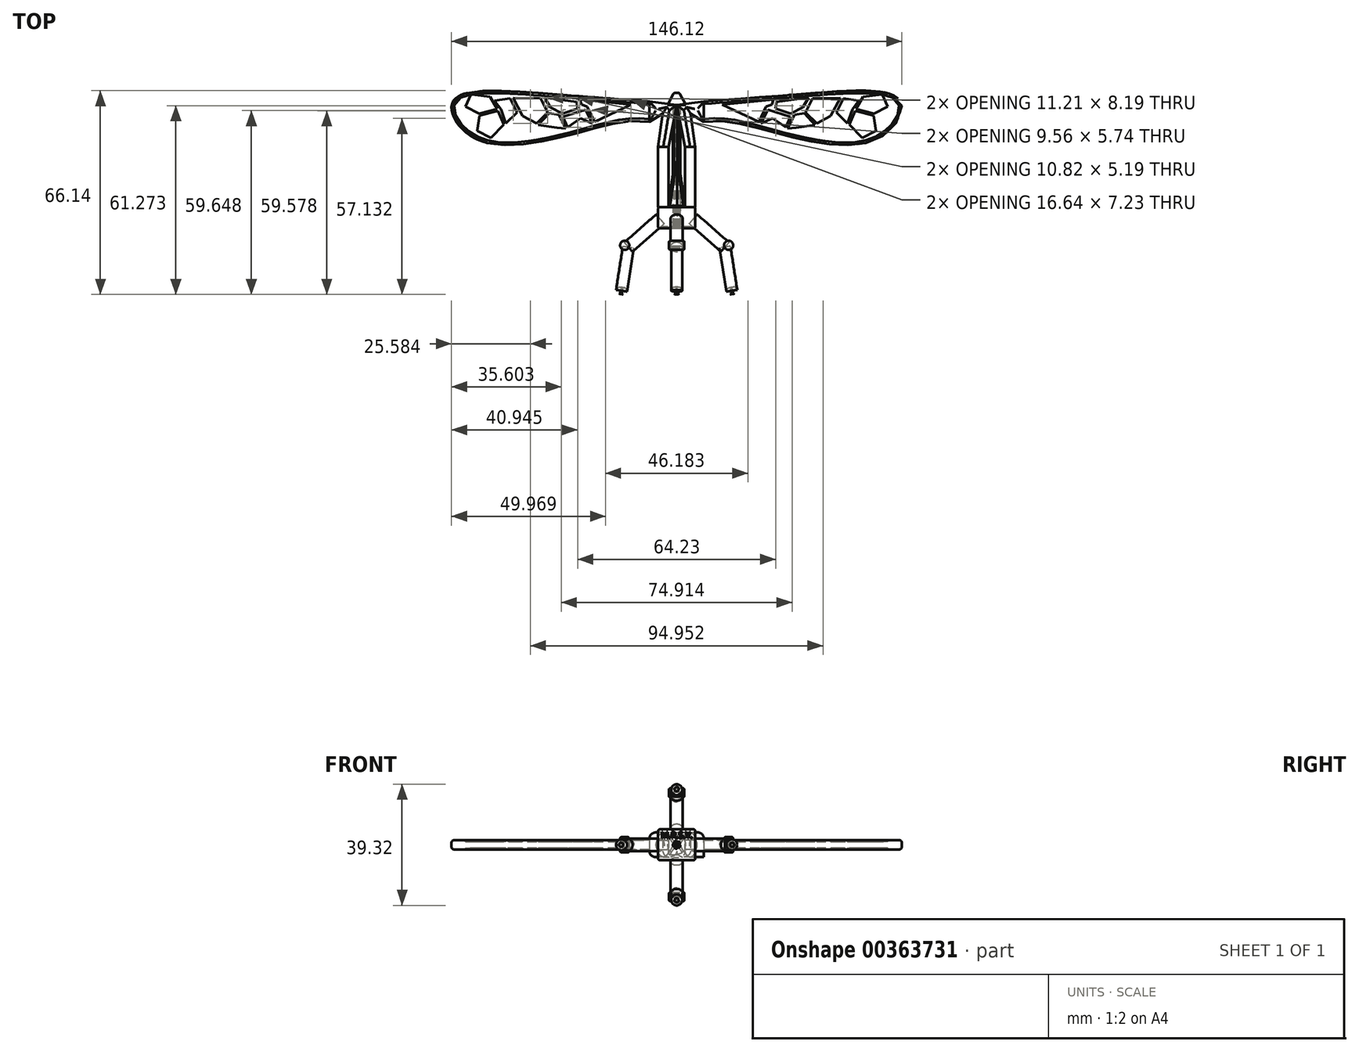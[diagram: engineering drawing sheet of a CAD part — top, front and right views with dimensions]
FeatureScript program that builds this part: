
annotation { "Feature Type Name" : "Feature", "Feature Type Description" : "" }
export const myFeature = defineFeature(function(context is Context, id is Id, definition is map)
    precondition{}
    {
        {
            var Q0;
            Q0=qCreatedBy(makeId("Top.planeOp"),FACE);
            var sketch = newSketch(context, id + "F0", { "sketchPlane" : qUnion([Q0])});
            skLineSegment(sketch, "E0.bottom", {"start": v(-6, 3.87) * mm, "end": v(0, 3.87) * mm});
            skLineSegment(sketch, "E0.top", {"start": v(-6, -3.02) * mm, "end": v(0, -3.02) * mm});
            skLineSegment(sketch, "E0.left", {"start": v(-6, 3.87) * mm, "end": v(-6, -3.02) * mm});
            skLineSegment(sketch, "E0.right", {"start": v(0, 3.87) * mm, "end": v(0, -3.02) * mm});
            skLineSegment(sketch, "E1", {"start": v(-6, 3.87) * mm, "end": v(-6, 23.41) * mm});
            skLineSegment(sketch, "E2", {"start": v(-6, 23.41) * mm, "end": v(-2.68, 23.41) * mm});
            skLineSegment(sketch, "E3", {"start": v(-2.68, 23.41) * mm, "end": v(-2.68, 3.87) * mm});
            skLineSegment(sketch, "E4", {"start": v(-6, 23.41) * mm, "end": v(-4.5, 34.28) * mm});
            skLineSegment(sketch, "E5", {"start": v(-4.5, 34.28) * mm, "end": v(-8.84, 31.63) * mm});
            skLineSegment(sketch, "E6", {"start": v(-8.84, 31.63) * mm, "end": v(-8.84, 38.19) * mm});
            skLineSegment(sketch, "E7", {"start": v(-8.84, 38.19) * mm, "end": v(0, 36.98) * mm});
            skLineSegment(sketch, "E8", {"start": v(-2.68, 23.41) * mm, "end": v(0, 36.98) * mm});
            skLineSegment(sketch, "E9.MirrorCS", {"start": v(6, 3.87) * mm, "end": v(0, 3.87) * mm});
            skLineSegment(sketch, "E10.MirrorCS", {"start": v(2.68, 23.41) * mm, "end": v(0, 36.98) * mm});
            skLineSegment(sketch, "E11.MirrorCS", {"start": v(6, -3.02) * mm, "end": v(0, -3.02) * mm});
            skLineSegment(sketch, "E12.MirrorCS", {"start": v(8.84, 38.19) * mm, "end": v(0, 36.98) * mm});
            skLineSegment(sketch, "E13.MirrorCS", {"start": v(6, 3.87) * mm, "end": v(6, -3.02) * mm});
            skLineSegment(sketch, "E14.MirrorCS", {"start": v(4.5, 34.28) * mm, "end": v(8.84, 31.63) * mm});
            skLineSegment(sketch, "E15.MirrorCS", {"start": v(8.84, 31.63) * mm, "end": v(8.84, 38.19) * mm});
            skLineSegment(sketch, "E16.MirrorCS", {"start": v(6, 23.41) * mm, "end": v(4.5, 34.28) * mm});
            skLineSegment(sketch, "E17.MirrorCS", {"start": v(6, 3.87) * mm, "end": v(6, 23.41) * mm});
            skLineSegment(sketch, "E18.MirrorCS", {"start": v(6, 23.41) * mm, "end": v(2.68, 23.41) * mm});
            skLineSegment(sketch, "E19.MirrorCS", {"start": v(2.68, 23.41) * mm, "end": v(2.68, 3.87) * mm});
            skFitSpline(sketch, "E20", {"points": [v(-8.84, 38.19) * mm, v(-45.9, 40.99) * mm, v(-72.58, 38.19) * mm, v(-63.04, 25.19) * mm, v(-19.97, 31.15) * mm, v(-8.84, 31.63) * mm], "startDerivative": vector(-146.25, 11.04) * mm, "endDerivative": vector(65.13, -7.24) * mm});
            skFitSpline(sketch, "E21.MirrorCS", {"points": [v(8.84, 38.19) * mm, v(45.9, 40.99) * mm, v(72.58, 38.19) * mm, v(63.04, 25.19) * mm, v(19.97, 31.15) * mm, v(8.84, 31.63) * mm], "startDerivative": vector(146.25, 11.04) * mm, "endDerivative": vector(-65.13, -7.24) * mm});
            skLineSegment(sketch, "E22", {"start": v(0, 3.87) * mm, "end": v(0, 18.7) * mm});
            skLineSegment(sketch, "E23", {"start": v(0, 18.7) * mm, "end": v(-0.65, 18.7) * mm});
            skLineSegment(sketch, "E24", {"start": v(0, 18.7) * mm, "end": v(0.65, 18.7) * mm});
            skLineSegment(sketch, "E25", {"start": v(-2.68, 3.87) * mm, "end": v(-0.65, 18.7) * mm});
            skLineSegment(sketch, "E26", {"start": v(2.68, 3.87) * mm, "end": v(0.65, 18.7) * mm});
            skSolve(sketch);
        }
        {
            var Q0;
            Q0=makeQuery(id+"F0.imprint","IMPRINT",FACE,{"disambiguationData":[TD([[makeQuery(id+"F0.imprint","IMPRINT",EDGE,{"derivedFrom":sQuery(id+"F0.wireOp",EDGE,"E2")}),1.0]])]});
            var Q1;
            Q1=makeQuery(id+"F0.imprint","IMPRINT",FACE,{"disambiguationData":[TD([[makeQuery(id+"F0.imprint","IMPRINT",EDGE,{"derivedFrom":sQuery(id+"F0.wireOp",EDGE,"E10.MirrorCS")}),-1.0]])]});
            extrude(context, id + "F1", {"entities" : qUnion([Q0, Q1]), "endBound" : BoundingType.SYMMETRIC, "depth" : 8 * mm});
        }
        {
            var Q0;
            {var subQ3=sQuery(id+"F0.wireOp",EDGE,"2m0UVoe8-9YMW-rYIg-5lbe-QnaoNtSdkHYh");Q0=makeQuery(id+"F0.imprint","IMPRINT",FACE,{"disambiguationData":[TD([[makeQuery(id+"F0.imprint","IMPRINT",EDGE,{"derivedFrom":subQ3}),-1.0]])]});}
            var Q1;
            {var subQ0=sQuery(id+"F0.wireOp",EDGE,"E1");Q1=makeQuery(id+"F0.imprint","IMPRINT",FACE,{"disambiguationData":[TD([[makeQuery(id+"F0.imprint","IMPRINT",EDGE,{"derivedFrom":subQ0}),-1.0]])]});}
            var Q2;
            {var subQ0=sQuery(id+"F0.wireOp",EDGE,"E17.MirrorCS");Q2=makeQuery(id+"F0.imprint","IMPRINT",FACE,{"disambiguationData":[TD([[makeQuery(id+"F0.imprint","IMPRINT",EDGE,{"derivedFrom":subQ0}),1.0]])]});}
            extrude(context, id + "F2", {"entities" : qUnion([Q0, Q1, Q2]), "endBound" : BoundingType.SYMMETRIC, "depth" : 3 * mm});
        }
        {
            var Q0;
            Q0=makeQuery(id+"F0.imprint","IMPRINT",FACE,{"disambiguationData":[TD([[makeQuery(id+"F0.imprint","IMPRINT",EDGE,{"derivedFrom":sQuery(id+"F0.wireOp",EDGE,"E0.top")}),1.0]])]});
            var Q1;
            Q1=makeQuery(id+"F0.imprint","IMPRINT",FACE,{"disambiguationData":[TD([[makeQuery(id+"F0.imprint","IMPRINT",EDGE,{"derivedFrom":sQuery(id+"F0.wireOp",EDGE,"E11.MirrorCS")}),-1.0]])]});
            extrude(context, id + "F3", {"entities" : qUnion([Q0, Q1]), "endBound" : BoundingType.SYMMETRIC, "depth" : 10 * mm});
        }
        {
            var Q0;
            {var subQ0=sQuery(id+"F0.wireOp",EDGE,"E22");Q0=makeQuery(id+"F0.imprint","IMPRINT",FACE,{"disambiguationData":[TD([[makeQuery(id+"F0.imprint","IMPRINT",EDGE,{"derivedFrom":subQ0}),1.0]])]});}
            var Q1;
            {var subQ0=sQuery(id+"F0.wireOp",EDGE,"E22");Q1=makeQuery(id+"F0.imprint","IMPRINT",FACE,{"disambiguationData":[TD([[makeQuery(id+"F0.imprint","IMPRINT",EDGE,{"derivedFrom":subQ0}),-1.0]])]});}
            var Q2;
            Q2=sQuery(id+"F0.wireOp",EDGE,"E24");
            revolve(context, id + "F4", {"entities" : qUnion([Q0, Q1]), "axis" : qUnion([Q2]), "revolveType" : RevolveType.SYMMETRIC, "angle" : 25 * degree});
        }
        {
            var Q0;
            Q0=makeQuery(id+"F3.opExtrude","SWEPT_FACE",FACE,{"disambiguationData":[OSD([sQuery(id+"F0.wireOp",EDGE,"E0.top"),sQuery(id+"F0.wireOp",EDGE,"E11.MirrorCS")])]});
            var sketch = newSketch(context, id + "F5", { "sketchPlane" : qUnion([Q0])});
            skCircle(sketch, "E27.cCircle", {"center": v(0, 0) * mm, "radius": 0.63 * mm, "construction": true});
            skLineSegment(sketch, "E27.0", {"start": v(-0.32, 0.7) * mm, "end": v(0.58, 0.52) * mm});
            skLineSegment(sketch, "E27.1", {"start": v(0.58, 0.52) * mm, "end": v(0.68, -0.39) * mm});
            skLineSegment(sketch, "E27.2", {"start": v(0.68, -0.39) * mm, "end": v(-0.16, -0.76) * mm});
            skLineSegment(sketch, "E27.3", {"start": v(-0.16, -0.76) * mm, "end": v(-0.77, -0.09) * mm});
            skLineSegment(sketch, "E27.4", {"start": v(-0.77, -0.09) * mm, "end": v(-0.32, 0.7) * mm});
            skPoint(sketch, "E27.0.midPoint", {"position": v(0.13, 0.62) * mm});
            skCircle(sketch, "E28", {"center": v(-0.77, -0.09) * mm, "radius": 0.5 * mm});
            skCircle(sketch, "E29", {"center": v(-0.16, -0.76) * mm, "radius": 0.5 * mm});
            skCircle(sketch, "E30", {"center": v(0.68, -0.39) * mm, "radius": 0.5 * mm});
            skCircle(sketch, "E31", {"center": v(0.58, 0.52) * mm, "radius": 0.5 * mm});
            skCircle(sketch, "E32", {"center": v(-0.32, 0.7) * mm, "radius": 0.5 * mm});
            skSolve(sketch);
        }
        {
            var Q0;
            {var subQ0=sQuery(id+"F5.wireOp",EDGE,"E27.3");var subQ1=sQuery(id+"F5.wireOp",EDGE,"E27.2");var subQ2=makeQuery(id+"F5.imprint","INTERSECT",VERTEX,{"derivedFrom":[subQ1,subQ0]});Q0=makeQuery(id+"F5.imprint","IMPRINT",FACE,{"disambiguationData":[TD([[makeQuery(id+"F5.imprint","IMPRINT",EDGE,{"disambiguationData":[TD([[subQ2,1.0]])],"derivedFrom":subQ1}),1.0]])]});}
            var Q1;
            {var subQ0=sQuery(id+"F5.wireOp",EDGE,"E27.3");var subQ1=sQuery(id+"F5.wireOp",EDGE,"E27.2");var subQ2=makeQuery(id+"F5.imprint","INTERSECT",VERTEX,{"derivedFrom":[subQ1,subQ0]});Q1=makeQuery(id+"F5.imprint","IMPRINT",FACE,{"disambiguationData":[TD([[makeQuery(id+"F5.imprint","IMPRINT",EDGE,{"disambiguationData":[TD([[subQ2,1.0]])],"derivedFrom":subQ1}),-1.0]])]});}
            var Q2;
            {var subQ0=sQuery(id+"F5.wireOp",EDGE,"E27.4");var subQ1=sQuery(id+"F5.wireOp",EDGE,"E27.3");var subQ2=makeQuery(id+"F5.imprint","INTERSECT",VERTEX,{"derivedFrom":[subQ1,subQ0]});Q2=makeQuery(id+"F5.imprint","IMPRINT",FACE,{"disambiguationData":[TD([[makeQuery(id+"F5.imprint","IMPRINT",EDGE,{"disambiguationData":[TD([[subQ2,1.0]])],"derivedFrom":subQ1}),1.0]])]});}
            var Q3;
            {var subQ0=sQuery(id+"F5.wireOp",EDGE,"E27.4");var subQ1=sQuery(id+"F5.wireOp",EDGE,"E27.3");var subQ2=makeQuery(id+"F5.imprint","INTERSECT",VERTEX,{"derivedFrom":[subQ1,subQ0]});Q3=makeQuery(id+"F5.imprint","IMPRINT",FACE,{"disambiguationData":[TD([[makeQuery(id+"F5.imprint","IMPRINT",EDGE,{"disambiguationData":[TD([[subQ2,1.0]])],"derivedFrom":subQ1}),-1.0]])]});}
            var Q4;
            {var subQ0=sQuery(id+"F5.wireOp",EDGE,"E27.4");var subQ1=sQuery(id+"F5.wireOp",EDGE,"E27.0");var subQ2=makeQuery(id+"F5.imprint","INTERSECT",VERTEX,{"derivedFrom":[subQ1,subQ0]});Q4=makeQuery(id+"F5.imprint","IMPRINT",FACE,{"disambiguationData":[TD([[makeQuery(id+"F5.imprint","IMPRINT",EDGE,{"disambiguationData":[TD([[subQ2,-1.0]])],"derivedFrom":subQ1}),1.0]])]});}
            var Q5;
            {var subQ0=sQuery(id+"F5.wireOp",EDGE,"E27.4");var subQ1=sQuery(id+"F5.wireOp",EDGE,"E27.0");var subQ2=makeQuery(id+"F5.imprint","INTERSECT",VERTEX,{"derivedFrom":[subQ1,subQ0]});Q5=makeQuery(id+"F5.imprint","IMPRINT",FACE,{"disambiguationData":[TD([[makeQuery(id+"F5.imprint","IMPRINT",EDGE,{"disambiguationData":[TD([[subQ2,-1.0]])],"derivedFrom":subQ1}),-1.0]])]});}
            var Q6;
            {var subQ0=sQuery(id+"F5.wireOp",EDGE,"E27.1");var subQ1=sQuery(id+"F5.wireOp",EDGE,"E27.0");var subQ2=makeQuery(id+"F5.imprint","INTERSECT",VERTEX,{"derivedFrom":[subQ1,subQ0]});Q6=makeQuery(id+"F5.imprint","IMPRINT",FACE,{"disambiguationData":[TD([[makeQuery(id+"F5.imprint","IMPRINT",EDGE,{"disambiguationData":[TD([[subQ2,1.0]])],"derivedFrom":subQ1}),1.0]])]});}
            var Q7;
            {var subQ0=sQuery(id+"F5.wireOp",EDGE,"E27.1");var subQ1=sQuery(id+"F5.wireOp",EDGE,"E27.0");var subQ2=makeQuery(id+"F5.imprint","INTERSECT",VERTEX,{"derivedFrom":[subQ1,subQ0]});Q7=makeQuery(id+"F5.imprint","IMPRINT",FACE,{"disambiguationData":[TD([[makeQuery(id+"F5.imprint","IMPRINT",EDGE,{"disambiguationData":[TD([[subQ2,1.0]])],"derivedFrom":subQ1}),-1.0]])]});}
            var Q8;
            {var subQ0=sQuery(id+"F5.wireOp",EDGE,"E27.2");var subQ1=sQuery(id+"F5.wireOp",EDGE,"E27.1");var subQ2=makeQuery(id+"F5.imprint","INTERSECT",VERTEX,{"derivedFrom":[subQ1,subQ0]});Q8=makeQuery(id+"F5.imprint","IMPRINT",FACE,{"disambiguationData":[TD([[makeQuery(id+"F5.imprint","IMPRINT",EDGE,{"disambiguationData":[TD([[subQ2,1.0]])],"derivedFrom":subQ1}),1.0]])]});}
            var Q9;
            {var subQ0=sQuery(id+"F5.wireOp",EDGE,"E27.2");var subQ1=sQuery(id+"F5.wireOp",EDGE,"E27.1");var subQ2=makeQuery(id+"F5.imprint","INTERSECT",VERTEX,{"derivedFrom":[subQ1,subQ0]});Q9=makeQuery(id+"F5.imprint","IMPRINT",FACE,{"disambiguationData":[TD([[makeQuery(id+"F5.imprint","IMPRINT",EDGE,{"disambiguationData":[TD([[subQ2,1.0]])],"derivedFrom":subQ1}),-1.0]])]});}
            extrude(context, id + "F6", {"entities" : qUnion([Q0, Q1, Q2, Q3, Q4, Q5, Q6, Q7, Q8, Q9]), "oppositeDirection" : true, "depth" : 40 * mm});
        }
        {
            var Q0;
            Q0=qCreatedBy(makeId("Top.planeOp"),FACE);
            var sketch = newSketch(context, id + "F7", { "sketchPlane" : qUnion([Q0])});
            skLineSegment(sketch, "E33", {"start": v(-5.36, 0) * mm, "end": v(-15.67, -9.06) * mm});
            skLineSegment(sketch, "E34", {"start": v(-15.67, -9.06) * mm, "end": v(-18.05, -24.33) * mm});
            skLineSegment(sketch, "E35", {"start": v(-18.05, -24.33) * mm, "end": v(-19.83, -24.05) * mm});
            skLineSegment(sketch, "E36", {"start": v(-15.67, -9.06) * mm, "end": v(-16.99, -7.56) * mm});
            skLineSegment(sketch, "E37", {"start": v(-15.67, -9.06) * mm, "end": v(-17.45, -8.78) * mm});
            skLineSegment(sketch, "E38", {"start": v(-19.83, -24.05) * mm, "end": v(-17.45, -8.78) * mm});
            skLineSegment(sketch, "E39", {"start": v(-5.36, 0) * mm, "end": v(-6.68, 1.5) * mm});
            skLineSegment(sketch, "E40", {"start": v(-16.99, -7.56) * mm, "end": v(-6.68, 1.5) * mm});
            skCircle(sketch, "E41", {"center": v(-16.87, -8.5) * mm, "radius": 1.49 * mm});
            skSolve(sketch);
        }
        {
            var Q0;
            Q0=makeQuery(id+"F7.imprint","IMPRINT",FACE,{"disambiguationData":[TD([[makeQuery(id+"F7.imprint","IMPRINT",EDGE,{"derivedFrom":sQuery(id+"F7.wireOp",EDGE,"E34")}),-1.0]])]});
            var Q1;
            Q1=sQuery(id+"F7.wireOp",EDGE,"E34");
            revolve(context, id + "F8", {"entities" : qUnion([Q0]), "axis" : qUnion([Q1]), "revolveType" : RevolveType.FULL});
        }
        {
            var Q0;
            Q0=makeQuery(id+"F7.imprint","IMPRINT",FACE,{"disambiguationData":[TD([[makeQuery(id+"F7.imprint","IMPRINT",EDGE,{"derivedFrom":sQuery(id+"F7.wireOp",EDGE,"E33")}),-1.0]])]});
            var Q1;
            Q1=sQuery(id+"F7.wireOp",EDGE,"E33");
            revolve(context, id + "F9", {"entities" : qUnion([Q0]), "axis" : qUnion([Q1]), "revolveType" : RevolveType.FULL});
        }
        {
            var Q0;
            {var subQ5=sQuery(id+"F7.wireOp",EDGE,"E36");Q0=makeQuery(id+"F7.imprint","IMPRINT",FACE,{"disambiguationData":[TD([[makeQuery(id+"F7.imprint","IMPRINT",EDGE,{"derivedFrom":subQ5}),1.0]])]});}
            var Q1;
            {var subQ0=sQuery(id+"F7.wireOp",EDGE,"E37");Q1=makeQuery(id+"F7.imprint","IMPRINT",FACE,{"disambiguationData":[TD([[makeQuery(id+"F7.imprint","IMPRINT",EDGE,{"derivedFrom":subQ0}),1.0]])]});}
            var Q2;
            {var subQ0=sQuery(id+"F7.wireOp",EDGE,"E36");Q2=makeQuery(id+"F7.imprint","IMPRINT",FACE,{"disambiguationData":[TD([[makeQuery(id+"F7.imprint","IMPRINT",EDGE,{"derivedFrom":subQ0}),-1.0]])]});}
            extrude(context, id + "F10", {"entities" : qUnion([Q0, Q1, Q2]), "endBound" : BoundingType.SYMMETRIC, "depth" : 5 * mm});
        }
        {
            var Q0;
            Q0=makeQuery(id+"F8.opRevolve","SWEPT_EDGE",EDGE,{"disambiguationData":[OSD([sQuery(id+"F7.wireOp",EDGE,"E35"),sQuery(id+"F7.wireOp",EDGE,"E38")])]});
            fillet(context, id + "F11", {"entities" : qUnion([Q0]), "radius" : 1.09 * mm, "tangentPropagation" : true, "allowEdgeOverflow" : false});
        }
        {
            var Q0;
            Q0=makeQuery(id+"F4.opRevolve","CAP_EDGE",EDGE,{"disambiguationData":[OSD([sQuery(id+"F0.wireOp",EDGE,"E25")])],"isStart":true});
            var Q1;
            Q1=makeQuery(id+"F4.opRevolve","CAP_EDGE",EDGE,{"disambiguationData":[OSD([sQuery(id+"F0.wireOp",EDGE,"E26")])],"isStart":true});
            var Q2;
            Q2=makeQuery(id+"F4.opRevolve","CAP_EDGE",EDGE,{"disambiguationData":[OSD([sQuery(id+"F0.wireOp",EDGE,"E26")])],"isStart":false});
            var Q3;
            Q3=makeQuery(id+"F4.opRevolve","CAP_EDGE",EDGE,{"disambiguationData":[OSD([sQuery(id+"F0.wireOp",EDGE,"E25")])],"isStart":false});
            var Q4;
            Q4=makeQuery(id+"F3.opExtrude","CAP_EDGE",EDGE,{"disambiguationData":[OSD([sQuery(id+"F0.wireOp",EDGE,"E0.bottom"),sQuery(id+"F0.wireOp",EDGE,"E9.MirrorCS")])],"isStart":true});
            var Q5;
            Q5=makeQuery(id+"F3.opExtrude","SWEPT_EDGE",EDGE,{"disambiguationData":[OSD([sQuery(id+"F0.wireOp",EDGE,"E9.MirrorCS"),sQuery(id+"F0.wireOp",EDGE,"E13.MirrorCS"),sQuery(id+"F0.wireOp",EDGE,"E17.MirrorCS")])]});
            var Q6;
            Q6=makeQuery(id+"F3.opExtrude","CAP_EDGE",EDGE,{"disambiguationData":[OSD([sQuery(id+"F0.wireOp",EDGE,"E0.bottom"),sQuery(id+"F0.wireOp",EDGE,"E9.MirrorCS")])],"isStart":false});
            var Q7;
            Q7=makeQuery(id+"F2.opExtrude","CAP_EDGE",EDGE,{"disambiguationData":[OSD([sQuery(id+"F0.wireOp",EDGE,"E17.MirrorCS")])],"isStart":false});
            var Q8;
            Q8=makeQuery(id+"F2.opExtrude","CAP_EDGE",EDGE,{"disambiguationData":[OSD([sQuery(id+"F0.wireOp",EDGE,"E17.MirrorCS")])],"isStart":true});
            var Q9;
            Q9=makeQuery(id+"F2.opExtrude","CAP_EDGE",EDGE,{"disambiguationData":[OSD([sQuery(id+"F0.wireOp",EDGE,"E19.MirrorCS")])],"isStart":true});
            var Q10;
            Q10=makeQuery(id+"F2.opExtrude","CAP_EDGE",EDGE,{"disambiguationData":[OSD([sQuery(id+"F0.wireOp",EDGE,"E19.MirrorCS")])],"isStart":false});
            var Q11;
            Q11=makeQuery(id+"F2.opExtrude","CAP_EDGE",EDGE,{"disambiguationData":[OSD([sQuery(id+"F0.wireOp",EDGE,"E3")])],"isStart":false});
            var Q12;
            Q12=makeQuery(id+"F2.opExtrude","CAP_EDGE",EDGE,{"disambiguationData":[OSD([sQuery(id+"F0.wireOp",EDGE,"E1")])],"isStart":false});
            var Q13;
            Q13=makeQuery(id+"F2.opExtrude","CAP_EDGE",EDGE,{"disambiguationData":[OSD([sQuery(id+"F0.wireOp",EDGE,"E1")])],"isStart":true});
            var Q14;
            Q14=makeQuery(id+"F2.opExtrude","CAP_EDGE",EDGE,{"disambiguationData":[OSD([sQuery(id+"F0.wireOp",EDGE,"E3")])],"isStart":true});
            var Q15;
            Q15=makeQuery(id+"F3.opExtrude","SWEPT_EDGE",EDGE,{"disambiguationData":[OSD([sQuery(id+"F0.wireOp",EDGE,"E0.bottom"),sQuery(id+"F0.wireOp",EDGE,"E0.left"),sQuery(id+"F0.wireOp",EDGE,"E1")])]});
            var Q16;
            Q16=makeQuery(id+"F3.opExtrude","CAP_EDGE",EDGE,{"disambiguationData":[OSD([sQuery(id+"F0.wireOp",EDGE,"E0.left")])],"isStart":false});
            var Q17;
            Q17=makeQuery(id+"F3.opExtrude","CAP_EDGE",EDGE,{"disambiguationData":[OSD([sQuery(id+"F0.wireOp",EDGE,"E0.top"),sQuery(id+"F0.wireOp",EDGE,"E11.MirrorCS")])],"isStart":false});
            var Q18;
            Q18=makeQuery(id+"F3.opExtrude","SWEPT_EDGE",EDGE,{"disambiguationData":[OSD([sQuery(id+"F0.wireOp",EDGE,"E11.MirrorCS"),sQuery(id+"F0.wireOp",EDGE,"E13.MirrorCS")])]});
            var Q19;
            Q19=makeQuery(id+"F3.opExtrude","CAP_EDGE",EDGE,{"disambiguationData":[OSD([sQuery(id+"F0.wireOp",EDGE,"E0.top"),sQuery(id+"F0.wireOp",EDGE,"E11.MirrorCS")])],"isStart":true});
            var Q20;
            Q20=makeQuery(id+"F3.opExtrude","SWEPT_EDGE",EDGE,{"disambiguationData":[OSD([sQuery(id+"F0.wireOp",EDGE,"E0.top"),sQuery(id+"F0.wireOp",EDGE,"E0.left")])]});
            var Q21;
            Q21=makeQuery(id+"F3.opExtrude","CAP_EDGE",EDGE,{"disambiguationData":[OSD([sQuery(id+"F0.wireOp",EDGE,"E13.MirrorCS")])],"isStart":false});
            var Q22;
            Q22=makeQuery(id+"F3.opExtrude","CAP_EDGE",EDGE,{"disambiguationData":[OSD([sQuery(id+"F0.wireOp",EDGE,"E13.MirrorCS")])],"isStart":true});
            var Q23;
            Q23=makeQuery(id+"F3.opExtrude","CAP_EDGE",EDGE,{"disambiguationData":[OSD([sQuery(id+"F0.wireOp",EDGE,"E0.left")])],"isStart":true});
            fillet(context, id + "F12", {"entities" : qUnion([Q0, Q1, Q2, Q3, Q4, Q5, Q6, Q7, Q8, Q9, Q10, Q11, Q12, Q13, Q14, Q15, Q16, Q17, Q18, Q19, Q20, Q21, Q22, Q23]), "radius" : 0.5 * mm, "tangentPropagation" : true, "allowEdgeOverflow" : false});
        }
        {
            var Q0;
            Q0=makeQuery(id+"F0.imprint","IMPRINT",FACE,{"disambiguationData":[TD([[makeQuery(id+"F0.imprint","IMPRINT",EDGE,{"derivedFrom":sQuery(id+"F0.wireOp",EDGE,"E15.MirrorCS")}),-1.0]])]});
            var Q1;
            Q1=makeQuery(id+"F0.imprint","IMPRINT",FACE,{"disambiguationData":[TD([[makeQuery(id+"F0.imprint","IMPRINT",EDGE,{"derivedFrom":sQuery(id+"F0.wireOp",EDGE,"E6")}),1.0]])]});
            extrude(context, id + "F13", {"entities" : qUnion([Q0, Q1]), "endBound" : BoundingType.SYMMETRIC, "depth" : 3 * mm});
        }
        {
            var Q0;
            Q0=makeQuery(id+"F13.opExtrude","CAP_FACE",FACE,{"disambiguationData":[OSD([sQuery(id+"F0.wireOp",EDGE,"E6"),sQuery(id+"F0.wireOp",EDGE,"E20")])],"isStart":false});
            var sketch = newSketch(context, id + "F14", { "sketchPlane" : qUnion([Q0])});
            skLineSegment(sketch, "E42.0", {"start": v(-44.14, 39.17) * mm, "end": v(-41.87, 34.66) * mm});
            skLineSegment(sketch, "E42.1", {"start": v(-41.87, 34.66) * mm, "end": v(-45.46, 31.11) * mm});
            skLineSegment(sketch, "E42.2", {"start": v(-45.46, 31.11) * mm, "end": v(-49.95, 33.43) * mm});
            skLineSegment(sketch, "E42.3", {"start": v(-49.95, 33.43) * mm, "end": v(-53.08, 39.3) * mm});
            skLineSegment(sketch, "E42.4", {"start": v(-53.08, 39.3) * mm, "end": v(-44.14, 39.17) * mm});
            skPoint(sketch, "E42.0.midPoint", {"position": v(-43, 36.92) * mm});
            skLineSegment(sketch, "E43.0", {"start": v(-38.24, 33.87) * mm, "end": v(-35.97, 29.36) * mm});
            skLineSegment(sketch, "E43.1", {"start": v(-35.97, 29.36) * mm, "end": v(-38.81, 29.65) * mm});
            skLineSegment(sketch, "E43.2", {"start": v(-38.81, 29.65) * mm, "end": v(-44.9, 30.58) * mm});
            skLineSegment(sketch, "E43.3", {"start": v(-44.9, 30.58) * mm, "end": v(-41.4, 34.32) * mm});
            skLineSegment(sketch, "E43.4", {"start": v(-41.4, 34.32) * mm, "end": v(-38.24, 33.87) * mm});
            skPoint(sketch, "E43.0.midPoint", {"position": v(-37.1, 31.62) * mm});
            skLineSegment(sketch, "E44.0", {"start": v(-32.46, 38.08) * mm, "end": v(-32.05, 35.9) * mm});
            skLineSegment(sketch, "E44.1", {"start": v(-32.05, 35.9) * mm, "end": v(-37.05, 34.24) * mm});
            skLineSegment(sketch, "E44.2", {"start": v(-37.05, 34.24) * mm, "end": v(-40.94, 36.24) * mm});
            skLineSegment(sketch, "E44.3", {"start": v(-40.94, 36.24) * mm, "end": v(-42.87, 39.43) * mm});
            skLineSegment(sketch, "E44.4", {"start": v(-42.87, 39.43) * mm, "end": v(-32.46, 38.08) * mm});
            skPoint(sketch, "E44.0.midPoint", {"position": v(-32.25, 37) * mm});
            skLineSegment(sketch, "E45.0", {"start": v(-14.77, 37.2) * mm, "end": v(-26.7, 31.52) * mm});
            skLineSegment(sketch, "E45.1", {"start": v(-26.7, 31.52) * mm, "end": v(-28.98, 36.58) * mm});
            skLineSegment(sketch, "E45.2", {"start": v(-28.98, 36.58) * mm, "end": v(-30.89, 37.1) * mm});
            skLineSegment(sketch, "E45.3", {"start": v(-30.89, 37.1) * mm, "end": v(-31.4, 38.75) * mm});
            skLineSegment(sketch, "E45.4", {"start": v(-31.4, 38.75) * mm, "end": v(-14.77, 37.2) * mm});
            skPoint(sketch, "E45.0.midPoint", {"position": v(-20.73, 34.36) * mm});
            skLineSegment(sketch, "E46.0", {"start": v(-29.6, 35.56) * mm, "end": v(-27.33, 31.05) * mm});
            skLineSegment(sketch, "E46.1", {"start": v(-27.33, 31.05) * mm, "end": v(-31.2, 32.68) * mm});
            skLineSegment(sketch, "E46.2", {"start": v(-31.2, 32.68) * mm, "end": v(-35.4, 29.82) * mm});
            skLineSegment(sketch, "E46.3", {"start": v(-35.4, 29.82) * mm, "end": v(-36.9, 33.27) * mm});
            skLineSegment(sketch, "E46.4", {"start": v(-36.9, 33.27) * mm, "end": v(-29.6, 35.56) * mm});
            skPoint(sketch, "E46.0.midPoint", {"position": v(-28.47, 33.3) * mm});
            skLineSegment(sketch, "E47.0", {"start": v(-57.94, 35.18) * mm, "end": v(-56.08, 30.67) * mm});
            skLineSegment(sketch, "E47.1", {"start": v(-56.08, 30.67) * mm, "end": v(-60.24, 26.3) * mm});
            skLineSegment(sketch, "E47.2", {"start": v(-60.24, 26.3) * mm, "end": v(-64.73, 28.62) * mm});
            skLineSegment(sketch, "E47.3", {"start": v(-64.73, 28.62) * mm, "end": v(-63.91, 33.6) * mm});
            skLineSegment(sketch, "E47.4", {"start": v(-63.91, 33.6) * mm, "end": v(-57.94, 35.18) * mm});
            skPoint(sketch, "E47.0.midPoint", {"position": v(-57.01, 32.93) * mm});
            skLineSegment(sketch, "E48.0", {"start": v(-54.1, 39.13) * mm, "end": v(-51.82, 34.62) * mm});
            skLineSegment(sketch, "E48.1", {"start": v(-51.82, 34.62) * mm, "end": v(-55.41, 31.07) * mm});
            skLineSegment(sketch, "E48.2", {"start": v(-55.41, 31.07) * mm, "end": v(-57.03, 35.63) * mm});
            skLineSegment(sketch, "E48.3", {"start": v(-57.03, 35.63) * mm, "end": v(-59.08, 38.37) * mm});
            skLineSegment(sketch, "E48.4", {"start": v(-59.08, 38.37) * mm, "end": v(-54.1, 39.13) * mm});
            skPoint(sketch, "E48.0.midPoint", {"position": v(-52.96, 36.88) * mm});
            skLineSegment(sketch, "E49.0", {"start": v(-60.54, 39.65) * mm, "end": v(-58.25, 35.78) * mm});
            skLineSegment(sketch, "E49.1", {"start": v(-58.25, 35.78) * mm, "end": v(-64.06, 34.23) * mm});
            skLineSegment(sketch, "E49.2", {"start": v(-64.06, 34.23) * mm, "end": v(-68.54, 36.55) * mm});
            skLineSegment(sketch, "E49.3", {"start": v(-68.54, 36.55) * mm, "end": v(-66.74, 40.47) * mm});
            skLineSegment(sketch, "E49.4", {"start": v(-66.74, 40.47) * mm, "end": v(-60.54, 39.65) * mm});
            skPoint(sketch, "E49.0.midPoint", {"position": v(-59.4, 37.72) * mm});
            skLineSegment(sketch, "E50.MirrorCS", {"start": v(57.03, 35.63) * mm, "end": v(59.08, 38.37) * mm});
            skLineSegment(sketch, "E51.MirrorCS", {"start": v(60.54, 39.65) * mm, "end": v(58.25, 35.78) * mm});
            skLineSegment(sketch, "E52.MirrorCS", {"start": v(40.94, 36.24) * mm, "end": v(42.87, 39.43) * mm});
            skLineSegment(sketch, "E53.MirrorCS", {"start": v(35.4, 29.82) * mm, "end": v(36.9, 33.27) * mm});
            skLineSegment(sketch, "E54.MirrorCS", {"start": v(27.33, 31.05) * mm, "end": v(31.2, 32.68) * mm});
            skLineSegment(sketch, "E55.MirrorCS", {"start": v(38.24, 33.87) * mm, "end": v(35.97, 29.36) * mm});
            skLineSegment(sketch, "E56.MirrorCS", {"start": v(35.97, 29.36) * mm, "end": v(38.81, 29.65) * mm});
            skLineSegment(sketch, "E57.MirrorCS", {"start": v(30.89, 37.1) * mm, "end": v(31.4, 38.75) * mm});
            skLineSegment(sketch, "E58.MirrorCS", {"start": v(68.54, 36.55) * mm, "end": v(66.74, 40.47) * mm});
            skLineSegment(sketch, "E59.MirrorCS", {"start": v(28.98, 36.58) * mm, "end": v(30.89, 37.1) * mm});
            skLineSegment(sketch, "E60.MirrorCS", {"start": v(51.82, 34.62) * mm, "end": v(55.41, 31.07) * mm});
            skLineSegment(sketch, "E61.MirrorCS", {"start": v(37.05, 34.24) * mm, "end": v(40.94, 36.24) * mm});
            skLineSegment(sketch, "E62.MirrorCS", {"start": v(41.4, 34.32) * mm, "end": v(38.24, 33.87) * mm});
            skLineSegment(sketch, "E63.MirrorCS", {"start": v(32.46, 38.08) * mm, "end": v(32.05, 35.9) * mm});
            skLineSegment(sketch, "E64.MirrorCS", {"start": v(54.1, 39.13) * mm, "end": v(51.82, 34.62) * mm});
            skLineSegment(sketch, "E65.MirrorCS", {"start": v(44.14, 39.17) * mm, "end": v(41.87, 34.66) * mm});
            skLineSegment(sketch, "E66.MirrorCS", {"start": v(49.95, 33.43) * mm, "end": v(53.08, 39.3) * mm});
            skLineSegment(sketch, "E67.MirrorCS", {"start": v(29.6, 35.56) * mm, "end": v(27.33, 31.05) * mm});
            skLineSegment(sketch, "E68.MirrorCS", {"start": v(57.94, 35.18) * mm, "end": v(56.08, 30.67) * mm});
            skLineSegment(sketch, "E69.MirrorCS", {"start": v(55.41, 31.07) * mm, "end": v(57.03, 35.63) * mm});
            skLineSegment(sketch, "E70.MirrorCS", {"start": v(26.7, 31.52) * mm, "end": v(28.98, 36.58) * mm});
            skLineSegment(sketch, "E71.MirrorCS", {"start": v(14.77, 37.2) * mm, "end": v(26.7, 31.52) * mm});
            skPoint(sketch, "E72.MirrorP", {"position": v(20.73, 34.36) * mm});
            skLineSegment(sketch, "E73.MirrorCS", {"start": v(42.87, 39.43) * mm, "end": v(32.46, 38.08) * mm});
            skLineSegment(sketch, "E74.MirrorCS", {"start": v(60.24, 26.3) * mm, "end": v(64.73, 28.62) * mm});
            skLineSegment(sketch, "E75.MirrorCS", {"start": v(64.06, 34.23) * mm, "end": v(68.54, 36.55) * mm});
            skLineSegment(sketch, "E76.MirrorCS", {"start": v(41.87, 34.66) * mm, "end": v(45.46, 31.11) * mm});
            skLineSegment(sketch, "E77.MirrorCS", {"start": v(31.4, 38.75) * mm, "end": v(14.77, 37.2) * mm});
            skLineSegment(sketch, "E78.MirrorCS", {"start": v(32.05, 35.9) * mm, "end": v(37.05, 34.24) * mm});
            skPoint(sketch, "E79.MirrorP", {"position": v(43, 36.92) * mm});
            skPoint(sketch, "E80.MirrorP", {"position": v(59.4, 37.72) * mm});
            skPoint(sketch, "E81.MirrorP", {"position": v(28.47, 33.3) * mm});
            skLineSegment(sketch, "E82.MirrorCS", {"start": v(31.2, 32.68) * mm, "end": v(35.4, 29.82) * mm});
            skPoint(sketch, "E83.MirrorP", {"position": v(57.01, 32.93) * mm});
            skLineSegment(sketch, "E84.MirrorCS", {"start": v(66.74, 40.47) * mm, "end": v(60.54, 39.65) * mm});
            skLineSegment(sketch, "E85.MirrorCS", {"start": v(36.9, 33.27) * mm, "end": v(29.6, 35.56) * mm});
            skLineSegment(sketch, "E86.MirrorCS", {"start": v(38.81, 29.65) * mm, "end": v(44.9, 30.58) * mm});
            skPoint(sketch, "E87.MirrorP", {"position": v(32.25, 37) * mm});
            skPoint(sketch, "E88.MirrorP", {"position": v(37.1, 31.62) * mm});
            skPoint(sketch, "E89.MirrorP", {"position": v(52.96, 36.88) * mm});
            skLineSegment(sketch, "E90.MirrorCS", {"start": v(45.46, 31.11) * mm, "end": v(49.95, 33.43) * mm});
            skLineSegment(sketch, "E91.MirrorCS", {"start": v(44.9, 30.58) * mm, "end": v(41.4, 34.32) * mm});
            skLineSegment(sketch, "E92.MirrorCS", {"start": v(63.91, 33.6) * mm, "end": v(57.94, 35.18) * mm});
            skLineSegment(sketch, "E93.MirrorCS", {"start": v(53.08, 39.3) * mm, "end": v(44.14, 39.17) * mm});
            skLineSegment(sketch, "E94.MirrorCS", {"start": v(58.25, 35.78) * mm, "end": v(64.06, 34.23) * mm});
            skLineSegment(sketch, "E95.MirrorCS", {"start": v(64.73, 28.62) * mm, "end": v(63.91, 33.6) * mm});
            skLineSegment(sketch, "E96.MirrorCS", {"start": v(56.08, 30.67) * mm, "end": v(60.24, 26.3) * mm});
            skLineSegment(sketch, "E97.MirrorCS", {"start": v(59.08, 38.37) * mm, "end": v(54.1, 39.13) * mm});
            skSolve(sketch);
        }
        {
            var Q0;
            Q0=makeQuery(id+"F14.imprint","IMPRINT",FACE,{"disambiguationData":[TD([[makeQuery(id+"F14.imprint","IMPRINT",EDGE,{"derivedFrom":sQuery(id+"F14.wireOp",EDGE,"E42.0")}),-1.0]])]});
            var Q1;
            Q1=makeQuery(id+"F14.imprint","IMPRINT",FACE,{"disambiguationData":[TD([[makeQuery(id+"F14.imprint","IMPRINT",EDGE,{"derivedFrom":sQuery(id+"F14.wireOp",EDGE,"E48.0")}),-1.0]])]});
            var Q2;
            Q2=makeQuery(id+"F14.imprint","IMPRINT",FACE,{"disambiguationData":[TD([[makeQuery(id+"F14.imprint","IMPRINT",EDGE,{"derivedFrom":sQuery(id+"F14.wireOp",EDGE,"E49.0")}),-1.0]])]});
            var Q3;
            Q3=makeQuery(id+"F14.imprint","IMPRINT",FACE,{"disambiguationData":[TD([[makeQuery(id+"F14.imprint","IMPRINT",EDGE,{"derivedFrom":sQuery(id+"F14.wireOp",EDGE,"E47.0")}),-1.0]])]});
            var Q4;
            Q4=makeQuery(id+"F14.imprint","IMPRINT",FACE,{"disambiguationData":[TD([[makeQuery(id+"F14.imprint","IMPRINT",EDGE,{"derivedFrom":sQuery(id+"F14.wireOp",EDGE,"E43.0")}),-1.0]])]});
            var Q5;
            Q5=makeQuery(id+"F14.imprint","IMPRINT",FACE,{"disambiguationData":[TD([[makeQuery(id+"F14.imprint","IMPRINT",EDGE,{"derivedFrom":sQuery(id+"F14.wireOp",EDGE,"E44.0")}),-1.0]])]});
            var Q6;
            Q6=makeQuery(id+"F14.imprint","IMPRINT",FACE,{"disambiguationData":[TD([[makeQuery(id+"F14.imprint","IMPRINT",EDGE,{"derivedFrom":sQuery(id+"F14.wireOp",EDGE,"E46.0")}),-1.0]])]});
            var Q7;
            Q7=makeQuery(id+"F14.imprint","IMPRINT",FACE,{"disambiguationData":[TD([[makeQuery(id+"F14.imprint","IMPRINT",EDGE,{"derivedFrom":sQuery(id+"F14.wireOp",EDGE,"E45.0")}),-1.0]])]});
            var Q8;
            Q8=makeQuery(id+"F14.imprint","IMPRINT",FACE,{"disambiguationData":[TD([[makeQuery(id+"F14.imprint","IMPRINT",EDGE,{"derivedFrom":sQuery(id+"F14.wireOp",EDGE,"E57.MirrorCS")}),1.0]])]});
            var Q9;
            Q9=makeQuery(id+"F14.imprint","IMPRINT",FACE,{"disambiguationData":[TD([[makeQuery(id+"F14.imprint","IMPRINT",EDGE,{"derivedFrom":sQuery(id+"F14.wireOp",EDGE,"E52.MirrorCS")}),1.0]])]});
            var Q10;
            Q10=makeQuery(id+"F14.imprint","IMPRINT",FACE,{"disambiguationData":[TD([[makeQuery(id+"F14.imprint","IMPRINT",EDGE,{"derivedFrom":sQuery(id+"F14.wireOp",EDGE,"E53.MirrorCS")}),1.0]])]});
            var Q11;
            Q11=makeQuery(id+"F14.imprint","IMPRINT",FACE,{"disambiguationData":[TD([[makeQuery(id+"F14.imprint","IMPRINT",EDGE,{"derivedFrom":sQuery(id+"F14.wireOp",EDGE,"E55.MirrorCS")}),1.0]])]});
            var Q12;
            Q12=makeQuery(id+"F14.imprint","IMPRINT",FACE,{"disambiguationData":[TD([[makeQuery(id+"F14.imprint","IMPRINT",EDGE,{"derivedFrom":sQuery(id+"F14.wireOp",EDGE,"E65.MirrorCS")}),1.0]])]});
            var Q13;
            Q13=makeQuery(id+"F14.imprint","IMPRINT",FACE,{"disambiguationData":[TD([[makeQuery(id+"F14.imprint","IMPRINT",EDGE,{"derivedFrom":sQuery(id+"F14.wireOp",EDGE,"E50.MirrorCS")}),1.0]])]});
            var Q14;
            Q14=makeQuery(id+"F14.imprint","IMPRINT",FACE,{"disambiguationData":[TD([[makeQuery(id+"F14.imprint","IMPRINT",EDGE,{"derivedFrom":sQuery(id+"F14.wireOp",EDGE,"E68.MirrorCS")}),1.0]])]});
            var Q15;
            Q15=makeQuery(id+"F14.imprint","IMPRINT",FACE,{"disambiguationData":[TD([[makeQuery(id+"F14.imprint","IMPRINT",EDGE,{"derivedFrom":sQuery(id+"F14.wireOp",EDGE,"E51.MirrorCS")}),1.0]])]});
            extrude(context, id + "F15", {"entities" : qUnion([Q0, Q1, Q2, Q3, Q4, Q5, Q6, Q7, Q8, Q9, Q10, Q11, Q12, Q13, Q14, Q15]), "operationType" : NewBodyOperationType.REMOVE, "oppositeDirection" : true, "depth" : 0.5 * mm});
        }
        {
            var Q0;
            Q0=qCreatedBy(makeId("Right.planeOp"),FACE);
            var sketch = newSketch(context, id + "F16", { "sketchPlane" : qUnion([Q0])});
            skLineSegment(sketch, "E98", {"start": v(36.98, 0) * mm, "end": v(36.98, 3) * mm});
            skLineSegment(sketch, "E99", {"start": v(36.98, 3) * mm, "end": v(40.98, 0.86) * mm});
            skLineSegment(sketch, "E100", {"start": v(40.98, 0.86) * mm, "end": v(40.98, 0) * mm});
            skLineSegment(sketch, "E101", {"start": v(40.98, 0) * mm, "end": v(36.98, 0) * mm});
            skSolve(sketch);
        }
        {
            var Q0;
            Q0=makeQuery(id+"F16.imprint","IMPRINT",FACE,{"disambiguationData":[TD([[makeQuery(id+"F16.imprint","IMPRINT",EDGE,{"derivedFrom":sQuery(id+"F16.wireOp",EDGE,"E98")}),-1.0]])]});
            var Q1;
            Q1=sQuery(id+"F16.wireOp",EDGE,"E101");
            revolve(context, id + "F17", {"entities" : qUnion([Q0]), "axis" : qUnion([Q1]), "revolveType" : RevolveType.FULL});
        }
        {
            var Q0;
            Q0=makeQuery(id+"F8.opRevolve","SWEPT_BODY",BODY,{"disambiguationData":[OSD([sQuery(id+"F7.wireOp",EDGE,"E34"),sQuery(id+"F7.wireOp",EDGE,"E35"),sQuery(id+"F7.wireOp",EDGE,"E37"),sQuery(id+"F7.wireOp",EDGE,"E38")])]});
            var Q1;
            Q1=qCreatedBy(makeId("Right.planeOp"),FACE);
            mirror(context, id + "F18", {"entities" : qUnion([Q0]), "mirrorPlane" : qUnion([Q1])});
        }
        {
            var Q0;
            Q0=makeQuery(id+"F9.opRevolve","SWEPT_BODY",BODY,{"disambiguationData":[OSD([sQuery(id+"F7.wireOp",EDGE,"E33"),sQuery(id+"F7.wireOp",EDGE,"E36"),sQuery(id+"F7.wireOp",EDGE,"E39"),sQuery(id+"F7.wireOp",EDGE,"E40")])]});
            var Q1;
            Q1=makeQuery(id+"F10.opExtrude","SWEPT_BODY",BODY,{"disambiguationData":[OSD([sQuery(id+"F7.wireOp",EDGE,"E33"),sQuery(id+"F7.wireOp",EDGE,"E34"),sQuery(id+"F7.wireOp",EDGE,"E41")])]});
            var Q2;
            Q2=qCreatedBy(makeId("Right.planeOp"),FACE);
            mirror(context, id + "F19", {"entities" : qUnion([Q0, Q1]), "mirrorPlane" : qUnion([Q2])});
        }
        {
            var Q0;
            Q0=makeQuery(id+"F19.opPattern","COPY",BODY,{"derivedFrom":makeQuery(id+"F9.opRevolve","SWEPT_BODY",BODY,{"disambiguationData":[OSD([sQuery(id+"F7.wireOp",EDGE,"E33"),sQuery(id+"F7.wireOp",EDGE,"E36"),sQuery(id+"F7.wireOp",EDGE,"E39"),sQuery(id+"F7.wireOp",EDGE,"E40")])]}),"instanceName":"1"});
            var Q1;
            Q1=makeQuery(id+"F18.opPattern","COPY",BODY,{"derivedFrom":makeQuery(id+"F8.opRevolve","SWEPT_BODY",BODY,{"disambiguationData":[OSD([sQuery(id+"F7.wireOp",EDGE,"E34"),sQuery(id+"F7.wireOp",EDGE,"E35"),sQuery(id+"F7.wireOp",EDGE,"E37"),sQuery(id+"F7.wireOp",EDGE,"E38")])]}),"instanceName":"1"});
            var Q2;
            Q2=makeQuery(id+"F19.opPattern","COPY",BODY,{"derivedFrom":makeQuery(id+"F10.opExtrude","SWEPT_BODY",BODY,{"disambiguationData":[OSD([sQuery(id+"F7.wireOp",EDGE,"E33"),sQuery(id+"F7.wireOp",EDGE,"E34"),sQuery(id+"F7.wireOp",EDGE,"E41")])]}),"instanceName":"1"});
            var Q3;
            Q3=makeQuery(id+"F10.opExtrude","SWEPT_BODY",BODY,{"disambiguationData":[OSD([sQuery(id+"F7.wireOp",EDGE,"E33"),sQuery(id+"F7.wireOp",EDGE,"E34"),sQuery(id+"F7.wireOp",EDGE,"E41")])]});
            var Q4;
            Q4=makeQuery(id+"F9.opRevolve","SWEPT_BODY",BODY,{"disambiguationData":[OSD([sQuery(id+"F7.wireOp",EDGE,"E33"),sQuery(id+"F7.wireOp",EDGE,"E36"),sQuery(id+"F7.wireOp",EDGE,"E39"),sQuery(id+"F7.wireOp",EDGE,"E40")])]});
            var Q5;
            Q5=makeQuery(id+"F8.opRevolve","SWEPT_BODY",BODY,{"disambiguationData":[OSD([sQuery(id+"F7.wireOp",EDGE,"E34"),sQuery(id+"F7.wireOp",EDGE,"E35"),sQuery(id+"F7.wireOp",EDGE,"E37"),sQuery(id+"F7.wireOp",EDGE,"E38")])]});
            transform(context, id + "F20", {"entities" : qUnion([Q0, Q1, Q2, Q3, Q4, Q5]), "transformType" : TransformType.COPY});
        }
        {
            var Q0;
            Q0=makeQuery(id+"F20.opPattern","COPY",BODY,{"derivedFrom":makeQuery(id+"F19.opPattern","COPY",BODY,{"derivedFrom":makeQuery(id+"F10.opExtrude","SWEPT_BODY",BODY,{"disambiguationData":[OSD([sQuery(id+"F7.wireOp",EDGE,"E33"),sQuery(id+"F7.wireOp",EDGE,"E34"),sQuery(id+"F7.wireOp",EDGE,"E41")])]}),"instanceName":"1"}),"instanceName":"1"});
            var Q1;
            Q1=makeQuery(id+"F20.opPattern","COPY",BODY,{"derivedFrom":makeQuery(id+"F19.opPattern","COPY",BODY,{"derivedFrom":makeQuery(id+"F9.opRevolve","SWEPT_BODY",BODY,{"disambiguationData":[OSD([sQuery(id+"F7.wireOp",EDGE,"E33"),sQuery(id+"F7.wireOp",EDGE,"E36"),sQuery(id+"F7.wireOp",EDGE,"E39"),sQuery(id+"F7.wireOp",EDGE,"E40")])]}),"instanceName":"1"}),"instanceName":"1"});
            var Q2;
            Q2=makeQuery(id+"F20.opPattern","COPY",BODY,{"derivedFrom":makeQuery(id+"F18.opPattern","COPY",BODY,{"derivedFrom":makeQuery(id+"F8.opRevolve","SWEPT_BODY",BODY,{"disambiguationData":[OSD([sQuery(id+"F7.wireOp",EDGE,"E34"),sQuery(id+"F7.wireOp",EDGE,"E35"),sQuery(id+"F7.wireOp",EDGE,"E37"),sQuery(id+"F7.wireOp",EDGE,"E38")])]}),"instanceName":"1"}),"instanceName":"1"});
            var Q3;
            Q3=makeQuery(id+"F20.opPattern","COPY",BODY,{"derivedFrom":makeQuery(id+"F10.opExtrude","SWEPT_BODY",BODY,{"disambiguationData":[OSD([sQuery(id+"F7.wireOp",EDGE,"E33"),sQuery(id+"F7.wireOp",EDGE,"E34"),sQuery(id+"F7.wireOp",EDGE,"E41")])]}),"instanceName":"1"});
            var Q4;
            Q4=makeQuery(id+"F20.opPattern","COPY",BODY,{"derivedFrom":makeQuery(id+"F9.opRevolve","SWEPT_BODY",BODY,{"disambiguationData":[OSD([sQuery(id+"F7.wireOp",EDGE,"E33"),sQuery(id+"F7.wireOp",EDGE,"E36"),sQuery(id+"F7.wireOp",EDGE,"E39"),sQuery(id+"F7.wireOp",EDGE,"E40")])]}),"instanceName":"1"});
            var Q5;
            Q5=makeQuery(id+"F20.opPattern","COPY",BODY,{"derivedFrom":makeQuery(id+"F8.opRevolve","SWEPT_BODY",BODY,{"disambiguationData":[OSD([sQuery(id+"F7.wireOp",EDGE,"E34"),sQuery(id+"F7.wireOp",EDGE,"E35"),sQuery(id+"F7.wireOp",EDGE,"E37"),sQuery(id+"F7.wireOp",EDGE,"E38")])]}),"instanceName":"1"});
            var Q6;
            Q6=sQuery(id+"F0.wireOp",EDGE,"E0.right");
            transform(context, id + "F21", {"entities" : qUnion([Q0, Q1, Q2, Q3, Q4, Q5]), "transformType" : TransformType.ROTATION, "transformAxis" : qUnion([Q6]), "angle" : 90 * degree, "makeCopy" : false});
        }
        {
            var Q0;
            Q0=makeQuery(id+"F13.opExtrude","CAP_FACE",FACE,{"disambiguationData":[OSD([sQuery(id+"F0.wireOp",EDGE,"E15.MirrorCS"),sQuery(id+"F0.wireOp",EDGE,"E21.MirrorCS")])],"isStart":true});
            var sketch = newSketch(context, id + "F22", { "sketchPlane" : qUnion([Q0])});
            skLineSegment(sketch, "E102.MirrorCS", {"start": v(-28.99, -36.58) * mm, "end": v(-30.89, -37.1) * mm});
            skLineSegment(sketch, "E103.MirrorCS", {"start": v(57.03, -35.63) * mm, "end": v(59.08, -38.37) * mm});
            skLineSegment(sketch, "E104.MirrorCS", {"start": v(30.89, -37.1) * mm, "end": v(31.4, -38.75) * mm});
            skLineSegment(sketch, "E105.MirrorCS", {"start": v(-27.33, -31.05) * mm, "end": v(-31.2, -32.68) * mm});
            skLineSegment(sketch, "E106.MirrorCS", {"start": v(35.4, -29.82) * mm, "end": v(36.9, -33.27) * mm});
            skLineSegment(sketch, "E107.MirrorCS", {"start": v(35.97, -29.36) * mm, "end": v(38.81, -29.65) * mm});
            skLineSegment(sketch, "E108.MirrorCS", {"start": v(27.33, -31.05) * mm, "end": v(31.2, -32.68) * mm});
            skLineSegment(sketch, "E109.MirrorCS", {"start": v(-68.55, -36.55) * mm, "end": v(-66.74, -40.47) * mm});
            skLineSegment(sketch, "E110.MirrorCS", {"start": v(68.54, -36.55) * mm, "end": v(66.74, -40.47) * mm});
            skLineSegment(sketch, "E111.MirrorCS", {"start": v(60.54, -39.65) * mm, "end": v(58.25, -35.78) * mm});
            skLineSegment(sketch, "E112.MirrorCS", {"start": v(-40.94, -36.24) * mm, "end": v(-42.87, -39.43) * mm});
            skLineSegment(sketch, "E113.MirrorCS", {"start": v(37.05, -34.24) * mm, "end": v(40.94, -36.24) * mm});
            skLineSegment(sketch, "E114.MirrorCS", {"start": v(-60.54, -39.65) * mm, "end": v(-58.25, -35.78) * mm});
            skLineSegment(sketch, "E115.MirrorCS", {"start": v(-32.46, -38.08) * mm, "end": v(-32.05, -35.9) * mm});
            skLineSegment(sketch, "E116.MirrorCS", {"start": v(-37.05, -34.24) * mm, "end": v(-40.94, -36.24) * mm});
            skLineSegment(sketch, "E117.MirrorCS", {"start": v(41.87, -34.66) * mm, "end": v(45.46, -31.11) * mm});
            skLineSegment(sketch, "E118.MirrorCS", {"start": v(-57.03, -35.63) * mm, "end": v(-59.08, -38.37) * mm});
            skLineSegment(sketch, "E119.MirrorCS", {"start": v(-30.89, -37.1) * mm, "end": v(-31.4, -38.75) * mm});
            skLineSegment(sketch, "E120.MirrorCS", {"start": v(-35.97, -29.36) * mm, "end": v(-38.81, -29.65) * mm});
            skLineSegment(sketch, "E121.MirrorCS", {"start": v(-38.24, -33.87) * mm, "end": v(-35.97, -29.36) * mm});
            skLineSegment(sketch, "E122.MirrorCS", {"start": v(-35.4, -29.82) * mm, "end": v(-36.9, -33.27) * mm});
            skLineSegment(sketch, "E123.MirrorCS", {"start": v(32.46, -38.08) * mm, "end": v(32.05, -35.9) * mm});
            skLineSegment(sketch, "E124.MirrorCS", {"start": v(-44.9, -30.58) * mm, "end": v(-41.4, -34.32) * mm});
            skLineSegment(sketch, "E125.MirrorCS", {"start": v(-41.4, -34.32) * mm, "end": v(-38.24, -33.87) * mm});
            skLineSegment(sketch, "E126.MirrorCS", {"start": v(28.98, -36.58) * mm, "end": v(30.89, -37.1) * mm});
            skLineSegment(sketch, "E127.MirrorCS", {"start": v(41.4, -34.32) * mm, "end": v(38.24, -33.87) * mm});
            skLineSegment(sketch, "E128.MirrorCS", {"start": v(40.94, -36.24) * mm, "end": v(42.87, -39.43) * mm});
            skLineSegment(sketch, "E129.MirrorCS", {"start": v(38.24, -33.87) * mm, "end": v(35.97, -29.36) * mm});
            skLineSegment(sketch, "E130.MirrorCS", {"start": v(55.41, -31.07) * mm, "end": v(57.03, -35.63) * mm});
            skLineSegment(sketch, "E131.MirrorCS", {"start": v(-54.1, -39.13) * mm, "end": v(-51.82, -34.62) * mm});
            skLineSegment(sketch, "E132.MirrorCS", {"start": v(54.1, -39.13) * mm, "end": v(51.82, -34.62) * mm});
            skLineSegment(sketch, "E133.MirrorCS", {"start": v(29.6, -35.56) * mm, "end": v(27.33, -31.05) * mm});
            skLineSegment(sketch, "E134.MirrorCS", {"start": v(-49.95, -33.43) * mm, "end": v(-53.08, -39.3) * mm});
            skLineSegment(sketch, "E135.MirrorCS", {"start": v(-32.05, -35.9) * mm, "end": v(-37.05, -34.24) * mm});
            skLineSegment(sketch, "E136.MirrorCS", {"start": v(49.95, -33.43) * mm, "end": v(53.08, -39.3) * mm});
            skLineSegment(sketch, "E137.MirrorCS", {"start": v(-57.94, -35.18) * mm, "end": v(-56.08, -30.67) * mm});
            skLineSegment(sketch, "E138.MirrorCS", {"start": v(44.14, -39.17) * mm, "end": v(41.87, -34.66) * mm});
            skLineSegment(sketch, "E139.MirrorCS", {"start": v(-26.7, -31.52) * mm, "end": v(-28.99, -36.58) * mm});
            skLineSegment(sketch, "E140.MirrorCS", {"start": v(-55.41, -31.07) * mm, "end": v(-57.03, -35.63) * mm});
            skLineSegment(sketch, "E141.MirrorCS", {"start": v(-44.14, -39.17) * mm, "end": v(-41.87, -34.66) * mm});
            skLineSegment(sketch, "E142.MirrorCS", {"start": v(57.94, -35.18) * mm, "end": v(56.08, -30.67) * mm});
            skLineSegment(sketch, "E143.MirrorCS", {"start": v(-29.6, -35.56) * mm, "end": v(-27.33, -31.05) * mm});
            skLineSegment(sketch, "E144.MirrorCS", {"start": v(26.7, -31.52) * mm, "end": v(28.98, -36.58) * mm});
            skPoint(sketch, "E145.MirrorP", {"position": v(-57.01, -32.93) * mm});
            skPoint(sketch, "E146.MirrorP", {"position": v(37.1, -31.62) * mm});
            skLineSegment(sketch, "E147.MirrorCS", {"start": v(32.05, -35.9) * mm, "end": v(37.05, -34.24) * mm});
            skLineSegment(sketch, "E148.MirrorCS", {"start": v(-60.24, -26.3) * mm, "end": v(-64.73, -28.62) * mm});
            skPoint(sketch, "E149.MirrorP", {"position": v(32.25, -37) * mm});
            skLineSegment(sketch, "E150.MirrorCS", {"start": v(31.2, -32.68) * mm, "end": v(35.4, -29.82) * mm});
            skLineSegment(sketch, "E151.MirrorCS", {"start": v(64.73, -28.62) * mm, "end": v(63.91, -33.6) * mm});
            skLineSegment(sketch, "E152.MirrorCS", {"start": v(14.77, -37.2) * mm, "end": v(26.7, -31.52) * mm});
            skPoint(sketch, "E153.MirrorP", {"position": v(28.47, -33.3) * mm});
            skLineSegment(sketch, "E154.MirrorCS", {"start": v(-64.06, -34.23) * mm, "end": v(-68.55, -36.55) * mm});
            skLineSegment(sketch, "E155.MirrorCS", {"start": v(58.25, -35.78) * mm, "end": v(64.06, -34.23) * mm});
            skLineSegment(sketch, "E156.MirrorCS", {"start": v(44.9, -30.58) * mm, "end": v(41.4, -34.32) * mm});
            skLineSegment(sketch, "E157.MirrorCS", {"start": v(-42.87, -39.43) * mm, "end": v(-32.46, -38.08) * mm});
            skLineSegment(sketch, "E158.MirrorCS", {"start": v(-14.77, -37.2) * mm, "end": v(-26.7, -31.52) * mm});
            skLineSegment(sketch, "E159.MirrorCS", {"start": v(64.06, -34.23) * mm, "end": v(68.54, -36.55) * mm});
            skPoint(sketch, "E160.MirrorP", {"position": v(-59.4, -37.72) * mm});
            skLineSegment(sketch, "E161.MirrorCS", {"start": v(31.4, -38.75) * mm, "end": v(14.77, -37.2) * mm});
            skPoint(sketch, "E162.MirrorP", {"position": v(43, -36.92) * mm});
            skLineSegment(sketch, "E163.MirrorCS", {"start": v(-31.4, -38.75) * mm, "end": v(-14.77, -37.2) * mm});
            skLineSegment(sketch, "E164.MirrorCS", {"start": v(-38.81, -29.65) * mm, "end": v(-44.9, -30.58) * mm});
            skPoint(sketch, "E165.MirrorP", {"position": v(20.73, -34.36) * mm});
            skLineSegment(sketch, "E166.MirrorCS", {"start": v(45.46, -31.11) * mm, "end": v(49.95, -33.43) * mm});
            skPoint(sketch, "E167.MirrorP", {"position": v(-20.73, -34.36) * mm});
            skLineSegment(sketch, "E168.MirrorCS", {"start": v(-59.08, -38.37) * mm, "end": v(-54.1, -39.13) * mm});
            skPoint(sketch, "E169.MirrorP", {"position": v(-37.1, -31.62) * mm});
            skLineSegment(sketch, "E170.MirrorCS", {"start": v(-66.74, -40.47) * mm, "end": v(-60.54, -39.65) * mm});
            skPoint(sketch, "E171.MirrorP", {"position": v(-32.25, -37) * mm});
            skLineSegment(sketch, "E172.MirrorCS", {"start": v(38.81, -29.65) * mm, "end": v(44.9, -30.58) * mm});
            skPoint(sketch, "E173.MirrorP", {"position": v(-28.47, -33.3) * mm});
            skLineSegment(sketch, "E174.MirrorCS", {"start": v(56.08, -30.67) * mm, "end": v(60.24, -26.3) * mm});
            skLineSegment(sketch, "E175.MirrorCS", {"start": v(53.08, -39.3) * mm, "end": v(44.14, -39.17) * mm});
            skLineSegment(sketch, "E176.MirrorCS", {"start": v(42.87, -39.43) * mm, "end": v(32.46, -38.08) * mm});
            skLineSegment(sketch, "E177.MirrorCS", {"start": v(66.74, -40.47) * mm, "end": v(60.54, -39.65) * mm});
            skPoint(sketch, "E178.MirrorP", {"position": v(57.01, -32.93) * mm});
            skPoint(sketch, "E179.MirrorP", {"position": v(-43, -36.92) * mm});
            skPoint(sketch, "E180.MirrorP", {"position": v(52.96, -36.88) * mm});
            skPoint(sketch, "E181.MirrorP", {"position": v(-52.96, -36.88) * mm});
            skLineSegment(sketch, "E182.MirrorCS", {"start": v(-41.87, -34.66) * mm, "end": v(-45.46, -31.11) * mm});
            skLineSegment(sketch, "E183.MirrorCS", {"start": v(-45.46, -31.11) * mm, "end": v(-49.95, -33.43) * mm});
            skLineSegment(sketch, "E184.MirrorCS", {"start": v(-53.08, -39.3) * mm, "end": v(-44.14, -39.17) * mm});
            skPoint(sketch, "E185.MirrorP", {"position": v(59.4, -37.72) * mm});
            skLineSegment(sketch, "E186.MirrorCS", {"start": v(36.9, -33.27) * mm, "end": v(29.6, -35.56) * mm});
            skLineSegment(sketch, "E187.MirrorCS", {"start": v(59.08, -38.37) * mm, "end": v(54.1, -39.13) * mm});
            skLineSegment(sketch, "E188.MirrorCS", {"start": v(60.24, -26.3) * mm, "end": v(64.73, -28.62) * mm});
            skLineSegment(sketch, "E189.MirrorCS", {"start": v(-51.82, -34.62) * mm, "end": v(-55.41, -31.07) * mm});
            skLineSegment(sketch, "E190.MirrorCS", {"start": v(-31.2, -32.68) * mm, "end": v(-35.4, -29.82) * mm});
            skLineSegment(sketch, "E191.MirrorCS", {"start": v(-36.9, -33.27) * mm, "end": v(-29.6, -35.56) * mm});
            skLineSegment(sketch, "E192.MirrorCS", {"start": v(51.82, -34.62) * mm, "end": v(55.41, -31.07) * mm});
            skLineSegment(sketch, "E193.MirrorCS", {"start": v(-56.08, -30.67) * mm, "end": v(-60.24, -26.3) * mm});
            skLineSegment(sketch, "E194.MirrorCS", {"start": v(-58.25, -35.78) * mm, "end": v(-64.06, -34.23) * mm});
            skLineSegment(sketch, "E195.MirrorCS", {"start": v(-64.73, -28.62) * mm, "end": v(-63.91, -33.6) * mm});
            skLineSegment(sketch, "E196.MirrorCS", {"start": v(63.91, -33.6) * mm, "end": v(57.94, -35.18) * mm});
            skLineSegment(sketch, "E197.MirrorCS", {"start": v(-63.91, -33.6) * mm, "end": v(-57.94, -35.18) * mm});
            skSolve(sketch);
        }
        {
            var Q0;
            Q0 = qSketchRegion(id + "F22", true);
            extrude(context, id + "F23", {"entities" : qUnion([Q0]), "operationType" : NewBodyOperationType.REMOVE, "oppositeDirection" : true, "depth" : 0.5 * mm});
        }
        {
            var Q0;
            Q0=makeQuery(id+"F1.opExtrude","CAP_EDGE",EDGE,{"disambiguationData":[OSD([sQuery(id+"F0.wireOp",EDGE,"E7")])],"isStart":false});
            var Q1;
            Q1=makeQuery(id+"F1.opExtrude","CAP_EDGE",EDGE,{"disambiguationData":[OSD([sQuery(id+"F0.wireOp",EDGE,"E12.MirrorCS")])],"isStart":false});
            var Q2;
            Q2=makeQuery(id+"F1.opExtrude","CAP_EDGE",EDGE,{"disambiguationData":[OSD([sQuery(id+"F0.wireOp",EDGE,"E12.MirrorCS")])],"isStart":true});
            var Q3;
            Q3=makeQuery(id+"F1.opExtrude","CAP_EDGE",EDGE,{"disambiguationData":[OSD([sQuery(id+"F0.wireOp",EDGE,"E7")])],"isStart":true});
            var Q4;
            Q4=makeQuery(id+"F1.opExtrude","CAP_EDGE",EDGE,{"disambiguationData":[OSD([sQuery(id+"F0.wireOp",EDGE,"E6")])],"isStart":true});
            var Q5;
            Q5=makeQuery(id+"F1.opExtrude","CAP_EDGE",EDGE,{"disambiguationData":[OSD([sQuery(id+"F0.wireOp",EDGE,"E5")])],"isStart":true});
            var Q6;
            Q6=makeQuery(id+"F1.opExtrude","CAP_EDGE",EDGE,{"disambiguationData":[OSD([sQuery(id+"F0.wireOp",EDGE,"E4")])],"isStart":true});
            var Q7;
            Q7=makeQuery(id+"F1.opExtrude","CAP_EDGE",EDGE,{"disambiguationData":[OSD([sQuery(id+"F0.wireOp",EDGE,"E10.MirrorCS")])],"isStart":true});
            var Q8;
            Q8=makeQuery(id+"F1.opExtrude","CAP_EDGE",EDGE,{"disambiguationData":[OSD([sQuery(id+"F0.wireOp",EDGE,"E16.MirrorCS")])],"isStart":true});
            var Q9;
            Q9=makeQuery(id+"F1.opExtrude","CAP_EDGE",EDGE,{"disambiguationData":[OSD([sQuery(id+"F0.wireOp",EDGE,"E14.MirrorCS")])],"isStart":true});
            var Q10;
            Q10=makeQuery(id+"F1.opExtrude","CAP_EDGE",EDGE,{"disambiguationData":[OSD([sQuery(id+"F0.wireOp",EDGE,"E14.MirrorCS")])],"isStart":false});
            var Q11;
            Q11=makeQuery(id+"F1.opExtrude","CAP_EDGE",EDGE,{"disambiguationData":[OSD([sQuery(id+"F0.wireOp",EDGE,"E16.MirrorCS")])],"isStart":false});
            var Q12;
            Q12=makeQuery(id+"F1.opExtrude","CAP_EDGE",EDGE,{"disambiguationData":[OSD([sQuery(id+"F0.wireOp",EDGE,"E15.MirrorCS")])],"isStart":false});
            var Q13;
            Q13=makeQuery(id+"F1.opExtrude","CAP_EDGE",EDGE,{"disambiguationData":[OSD([sQuery(id+"F0.wireOp",EDGE,"E6")])],"isStart":false});
            var Q14;
            Q14=makeQuery(id+"F1.opExtrude","CAP_EDGE",EDGE,{"disambiguationData":[OSD([sQuery(id+"F0.wireOp",EDGE,"E5")])],"isStart":false});
            var Q15;
            Q15=makeQuery(id+"F1.opExtrude","CAP_EDGE",EDGE,{"disambiguationData":[OSD([sQuery(id+"F0.wireOp",EDGE,"E4")])],"isStart":false});
            var Q16;
            Q16=makeQuery(id+"F1.opExtrude","CAP_EDGE",EDGE,{"disambiguationData":[OSD([sQuery(id+"F0.wireOp",EDGE,"E10.MirrorCS")])],"isStart":false});
            var Q17;
            Q17=makeQuery(id+"F1.opExtrude","CAP_EDGE",EDGE,{"disambiguationData":[OSD([sQuery(id+"F0.wireOp",EDGE,"E8")])],"isStart":false});
            var Q18;
            Q18=makeQuery(id+"F1.opExtrude","CAP_EDGE",EDGE,{"disambiguationData":[OSD([sQuery(id+"F0.wireOp",EDGE,"E8")])],"isStart":true});
            fillet(context, id + "F24", {"entities" : qUnion([Q0, Q1, Q2, Q3, Q4, Q5, Q6, Q7, Q8, Q9, Q10, Q11, Q12, Q13, Q14, Q15, Q16, Q17, Q18]), "radius" : 2 * mm, "tangentPropagation" : true, "allowEdgeOverflow" : false});
        }
        {
            var Q0;
            Q0=makeQuery(id+"F13.opExtrude","CAP_EDGE",EDGE,{"disambiguationData":[OSD([sQuery(id+"F0.wireOp",EDGE,"E21.MirrorCS")])],"isStart":true});
            var Q1;
            Q1=makeQuery(id+"F13.opExtrude","CAP_EDGE",EDGE,{"disambiguationData":[OSD([sQuery(id+"F0.wireOp",EDGE,"E21.MirrorCS")])],"isStart":false});
            var Q2;
            Q2=makeQuery(id+"F13.opExtrude","CAP_EDGE",EDGE,{"disambiguationData":[OSD([sQuery(id+"F0.wireOp",EDGE,"E20")])],"isStart":true});
            var Q3;
            Q3=makeQuery(id+"F13.opExtrude","CAP_EDGE",EDGE,{"disambiguationData":[OSD([sQuery(id+"F0.wireOp",EDGE,"E20")])],"isStart":false});
            fillet(context, id + "F25", {"entities" : qUnion([Q0, Q1, Q2, Q3]), "radius" : 0.8 * mm, "tangentPropagation" : true, "allowEdgeOverflow" : false});
        }
        {
            var Q0;
            Q0=makeQuery(id+"F17.opRevolve","SWEPT_EDGE",EDGE,{"disambiguationData":[OSD([sQuery(id+"F16.wireOp",EDGE,"E99"),sQuery(id+"F16.wireOp",EDGE,"E100")])]});
            fillet(context, id + "F26", {"entities" : qUnion([Q0]), "radius" : 0.66 * mm, "tangentPropagation" : true, "allowEdgeOverflow" : false});
        }
        {
            var Q0;
            Q0=makeQuery(id+"F19.opPattern","COPY",EDGE,{"derivedFrom":makeQuery(id+"F10.opExtrude","CAP_EDGE",EDGE,{"disambiguationData":[OSD([sQuery(id+"F7.wireOp",EDGE,"E41")])],"isStart":true}),"instanceName":"1"});
            var Q1;
            Q1=makeQuery(id+"F19.opPattern","COPY",EDGE,{"derivedFrom":makeQuery(id+"F10.opExtrude","CAP_EDGE",EDGE,{"disambiguationData":[OSD([sQuery(id+"F7.wireOp",EDGE,"E41")])],"isStart":false}),"instanceName":"1"});
            var Q2;
            Q2=makeQuery(id+"F20.opPattern","COPY",EDGE,{"derivedFrom":makeQuery(id+"F19.opPattern","COPY",EDGE,{"derivedFrom":makeQuery(id+"F10.opExtrude","CAP_EDGE",EDGE,{"disambiguationData":[OSD([sQuery(id+"F7.wireOp",EDGE,"E41")])],"isStart":true}),"instanceName":"1"}),"instanceName":"1"});
            var Q3;
            Q3=makeQuery(id+"F20.opPattern","COPY",EDGE,{"derivedFrom":makeQuery(id+"F19.opPattern","COPY",EDGE,{"derivedFrom":makeQuery(id+"F10.opExtrude","CAP_EDGE",EDGE,{"disambiguationData":[OSD([sQuery(id+"F7.wireOp",EDGE,"E41")])],"isStart":false}),"instanceName":"1"}),"instanceName":"1"});
            var Q4;
            Q4=makeQuery(id+"F10.opExtrude","CAP_EDGE",EDGE,{"disambiguationData":[OSD([sQuery(id+"F7.wireOp",EDGE,"E41")])],"isStart":true});
            var Q5;
            Q5=makeQuery(id+"F10.opExtrude","CAP_EDGE",EDGE,{"disambiguationData":[OSD([sQuery(id+"F7.wireOp",EDGE,"E41")])],"isStart":false});
            var Q6;
            Q6=makeQuery(id+"F20.opPattern","COPY",EDGE,{"derivedFrom":makeQuery(id+"F10.opExtrude","CAP_EDGE",EDGE,{"disambiguationData":[OSD([sQuery(id+"F7.wireOp",EDGE,"E41")])],"isStart":false}),"instanceName":"1"});
            var Q7;
            Q7=makeQuery(id+"F20.opPattern","COPY",EDGE,{"derivedFrom":makeQuery(id+"F10.opExtrude","CAP_EDGE",EDGE,{"disambiguationData":[OSD([sQuery(id+"F7.wireOp",EDGE,"E41")])],"isStart":true}),"instanceName":"1"});
            fillet(context, id + "F27", {"entities" : qUnion([Q0, Q1, Q2, Q3, Q4, Q5, Q6, Q7]), "radius" : 0.5 * mm, "tangentPropagation" : true, "allowEdgeOverflow" : false});
        }
        {
            var Q0;
            Q0=makeQuery(id+"F3.opExtrude","SWEPT_FACE",FACE,{"disambiguationData":[OSD([sQuery(id+"F0.wireOp",EDGE,"E0.top"),sQuery(id+"F0.wireOp",EDGE,"E11.MirrorCS")])]});
            var sketch = newSketch(context, id + "F28", { "sketchPlane" : qUnion([Q0])});
            skText(sketch, "E198", { "text": "M.R.S.V.", "fontName": "OpenSans-Regular.ttf"});
            const initialGuessF28  = {"E198": [-0.00512, 0.00214, 1, 0, 0.002]};
            skSetInitialGuess(sketch, initialGuessF28);
            skSolve(sketch);
        }
        {
            var Q0;
            Q0 = qSketchRegion(id + "F28", true);
            extrude(context, id + "F29", {"entities" : qUnion([Q0]), "operationType" : NewBodyOperationType.REMOVE, "oppositeDirection" : true, "depth" : 0.5 * mm});
        }
    });
